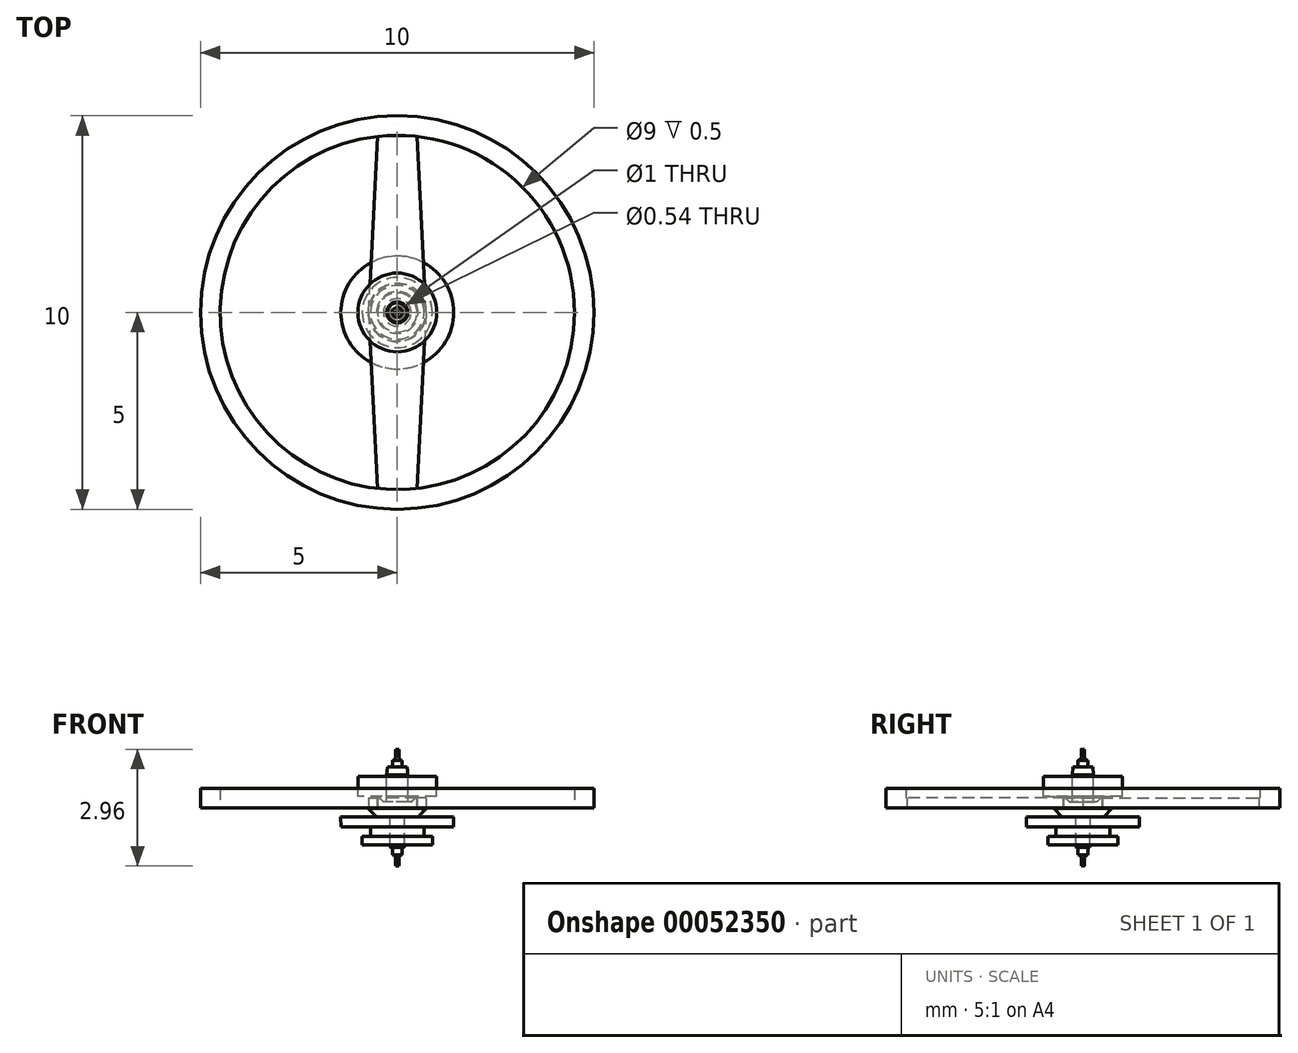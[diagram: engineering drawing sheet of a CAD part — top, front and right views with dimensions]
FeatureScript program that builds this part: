
annotation { "Feature Type Name" : "Feature", "Feature Type Description" : "" }
export const myFeature = defineFeature(function(context is Context, id is Id, definition is map)
    precondition{}
    {
        {
            var Q0;
            Q0=qCreatedBy(makeId("Front.planeOp"),FACE);
            var sketch = newSketch(context, id + "F0", { "sketchPlane" : qUnion([Q0])});
            skLineSegment(sketch, "E0", {"start": v(0, 0) * mm, "end": v(-0.04, 0) * mm});
            skLineSegment(sketch, "E1", {"start": v(-0.04, 0) * mm, "end": v(-0.04, 0.28) * mm});
            skLineSegment(sketch, "E2", {"start": v(-0.04, 0.28) * mm, "end": v(-0.12, 0.28) * mm});
            skLineSegment(sketch, "E3", {"start": v(-0.13, 0.28) * mm, "end": v(-0.13, 0.47) * mm});
            skLineSegment(sketch, "E4", {"start": v(-0.12, 0.47) * mm, "end": v(-0.17, 0.47) * mm});
            skLineSegment(sketch, "E5", {"start": v(-0.18, 0.48) * mm, "end": v(-0.18, 1.25) * mm});
            skLineSegment(sketch, "E6", {"start": v(-0.18, 1.25) * mm, "end": v(-0.53, 1.25) * mm});
            skLineSegment(sketch, "E7", {"start": v(-0.53, 1.25) * mm, "end": v(-0.74, 1.46) * mm});
            skLineSegment(sketch, "E8", {"start": v(-0.73, 1.47) * mm, "end": v(-0.5, 1.47) * mm});
            skLineSegment(sketch, "E9", {"start": v(-0.5, 1.47) * mm, "end": v(-0.5, 1.77) * mm});
            skLineSegment(sketch, "E10", {"start": v(-0.5, 1.77) * mm, "end": v(-0.35, 1.62) * mm});
            skLineSegment(sketch, "E11", {"start": v(-0.35, 1.62) * mm, "end": v(-0.27, 1.62) * mm});
            skLineSegment(sketch, "E12", {"start": v(-0.27, 1.62) * mm, "end": v(-0.27, 2.31) * mm});
            skLineSegment(sketch, "E13", {"start": v(-0.27, 2.3) * mm, "end": v(-0.25, 2.51) * mm});
            skLineSegment(sketch, "E14", {"start": v(-0.25, 2.51) * mm, "end": v(-0.12, 2.51) * mm});
            skLineSegment(sketch, "E15", {"start": v(-0.13, 2.51) * mm, "end": v(-0.13, 2.68) * mm});
            skLineSegment(sketch, "E16", {"start": v(-0.12, 2.68) * mm, "end": v(-0.04, 2.68) * mm});
            skLineSegment(sketch, "E17", {"start": v(-0.04, 2.68) * mm, "end": v(-0.04, 2.96) * mm});
            skLineSegment(sketch, "E18", {"start": v(-0.04, 2.96) * mm, "end": v(0, 2.96) * mm});
            skLineSegment(sketch, "E19", {"start": v(0, 2.96) * mm, "end": v(0, 0) * mm});
            skLineSegment(sketch, "E20", {"start": v(-0.73, 1.47) * mm, "end": v(-0.74, 1.46) * mm});
            skPoint(sketch, "E21.orphan", {"position": v(-0.75, 1.47) * mm});
            skLineSegment(sketch, "E22", {"start": v(-0.18, 0.48) * mm, "end": v(-0.17, 0.47) * mm});
            skPoint(sketch, "E23.orphan", {"position": v(-0.18, 0.47) * mm});
            skLineSegment(sketch, "E24", {"start": v(-0.27, 1.77) * mm, "end": v(-1, 1.77) * mm});
            skLineSegment(sketch, "E25", {"start": v(-1, 1.77) * mm, "end": v(-1, 2.27) * mm});
            skLineSegment(sketch, "E26", {"start": v(-1, 2.27) * mm, "end": v(-0.27, 2.27) * mm});
            skLineSegment(sketch, "E27", {"start": v(-0.18, 1.25) * mm, "end": v(-1.43, 1.24) * mm});
            skLineSegment(sketch, "E28", {"start": v(-1.43, 1.24) * mm, "end": v(-1.43, 1) * mm});
            skLineSegment(sketch, "E29", {"start": v(-1.43, 1) * mm, "end": v(-0.68, 1) * mm});
            skLineSegment(sketch, "E30", {"start": v(-0.68, 1) * mm, "end": v(-0.68, 0.75) * mm});
            skLineSegment(sketch, "E31", {"start": v(-0.68, 0.75) * mm, "end": v(-0.9, 0.75) * mm});
            skLineSegment(sketch, "E32", {"start": v(-0.9, 0.75) * mm, "end": v(-0.9, 0.54) * mm});
            skLineSegment(sketch, "E33", {"start": v(-0.9, 0.54) * mm, "end": v(-0.18, 0.54) * mm});
            skSolve(sketch);
        }
        {
            var Q0;
            Q0=makeQuery(id+"F0.imprint","IMPRINT",FACE,{"disambiguationData":[TD([[makeQuery(id+"F0.imprint","IMPRINT",EDGE,{"derivedFrom":sQuery(id+"F0.wireOp",EDGE,"E0")}),-1.0]])]});
            var Q1;
            Q1=sQuery(id+"F0.wireOp",EDGE,"E19");
            revolve(context, id + "F1", {"entities" : qUnion([Q0]), "axis" : qUnion([Q1]), "revolveType" : RevolveType.FULL});
        }
        {
            var Q0;
            Q0=makeQuery(id+"F1.opRevolve","SWEPT_EDGE",EDGE,{"disambiguationData":[OSD([sQuery(id+"F0.wireOp",EDGE,"E16"),sQuery(id+"F0.wireOp",EDGE,"E17")])]});
            fillet(context, id + "F2", {"entities" : qUnion([Q0]), "radius" : 0.1 * mm, "tangentPropagation" : true, "allowEdgeOverflow" : false});
        }
        {
            var Q0;
            Q0=makeQuery(id+"F1.opRevolve","SWEPT_EDGE",EDGE,{"disambiguationData":[OSD([sQuery(id+"F0.wireOp",EDGE,"E1"),sQuery(id+"F0.wireOp",EDGE,"E2")])]});
            fillet(context, id + "F3", {"entities" : qUnion([Q0]), "radius" : 0.1 * mm, "tangentPropagation" : true, "allowEdgeOverflow" : false});
        }
        {
            var Q0;
            Q0=makeQuery(id+"F1.opRevolve","SWEPT_FACE",FACE,{"disambiguationData":[OSD([sQuery(id+"F0.wireOp",EDGE,"E8")])]});
            var sketch = newSketch(context, id + "F4", { "sketchPlane" : qUnion([Q0])});
            skCircle(sketch, "E34.0", {"center": v(0, 0) * mm, "radius": 0.5 * mm});
            skCircle(sketch, "E35", {"center": v(0, 0) * mm, "radius": 5 * mm});
            skCircle(sketch, "E36", {"center": v(0, 0) * mm, "radius": 4.5 * mm});
            skCircle(sketch, "E37.0", {"center": v(0, 0) * mm, "radius": 0.73 * mm});
            skCircle(sketch, "E38", {"center": v(0, -4.5) * mm, "radius": 0.5 * mm, "construction": true});
            skCircle(sketch, "E39", {"center": v(0, 4.5) * mm, "radius": 0.5 * mm, "construction": true});
            skLineSegment(sketch, "E40", {"start": v(-0.73, 0) * mm, "end": v(-0.5, -4.47) * mm});
            skLineSegment(sketch, "E41", {"start": v(0.73, 0) * mm, "end": v(0.5, -4.47) * mm});
            skLineSegment(sketch, "E42", {"start": v(-0.73, 0) * mm, "end": v(-0.5, 4.47) * mm});
            skLineSegment(sketch, "E43", {"start": v(0.73, 0) * mm, "end": v(0.5, 4.47) * mm});
            skSolve(sketch);
        }
        {
            var Q0;
            Q0=makeQuery(id+"F4.imprint","IMPRINT",FACE,{"disambiguationData":[TD([[makeQuery(id+"F4.imprint","IMPRINT",EDGE,{"derivedFrom":sQuery(id+"F4.wireOp",EDGE,"E35")}),1.0]])]});
            var Q1;
            {var subQ0=sQuery(id+"F4.wireOp",EDGE,"6afa0338-6ddc-483a-af36-2ee9739ef733");var subQ1=sQuery(id+"F4.wireOp",EDGE,"E36");var subQ2=makeQuery(id+"F4.imprint","INTERSECT",VERTEX,{"derivedFrom":[subQ1,subQ0]});Q1=makeQuery(id+"F4.imprint","IMPRINT",FACE,{"disambiguationData":[TD([[makeQuery(id+"F4.imprint","IMPRINT",EDGE,{"disambiguationData":[TD([[subQ2,1.0]])],"derivedFrom":subQ1}),1.0]])]});}
            var Q2;
            {var subQ0=sQuery(id+"F4.wireOp",EDGE,"6afa0338-6ddc-483a-af36-2ee9739ef733");var subQ1=sQuery(id+"F4.wireOp",EDGE,"7b0f4a41-d3ac-4313-a1fa-f4f4589f324b");var subQ2=makeQuery(id+"F4.imprint","INTERSECT",VERTEX,{"derivedFrom":[subQ1,subQ0]});Q2=makeQuery(id+"F4.imprint","IMPRINT",FACE,{"disambiguationData":[TD([[makeQuery(id+"F4.imprint","IMPRINT",EDGE,{"disambiguationData":[TD([[subQ2,1.0]])],"derivedFrom":subQ1}),1.0]])]});}
            var Q3;
            {var subQ0=sQuery(id+"F4.wireOp",EDGE,"6afa0338-6ddc-483a-af36-2ee9739ef733");var subQ1=sQuery(id+"F4.wireOp",EDGE,"E34.0");var subQ2=makeQuery(id+"F4.imprint","INTERSECT",VERTEX,{"derivedFrom":[subQ1,subQ0,sQuery(id+"F4.wireOp",EDGE,"c907ba59-9a1e-415d-8a9b-9e27a359e78b")]});Q3=makeQuery(id+"F4.imprint","IMPRINT",FACE,{"disambiguationData":[TD([[makeQuery(id+"F4.imprint","IMPRINT",EDGE,{"disambiguationData":[TD([[subQ2,1.0]])],"derivedFrom":subQ1}),-1.0]])]});}
            var Q4;
            {var subQ0=sQuery(id+"F4.wireOp",EDGE,"80b41425-46ce-433e-b179-6af53ed49cd5");var subQ1=sQuery(id+"F4.wireOp",EDGE,"7b0f4a41-d3ac-4313-a1fa-f4f4589f324b");var subQ2=makeQuery(id+"F4.imprint","INTERSECT",VERTEX,{"derivedFrom":[subQ1,subQ0]});Q4=makeQuery(id+"F4.imprint","IMPRINT",FACE,{"disambiguationData":[TD([[makeQuery(id+"F4.imprint","IMPRINT",EDGE,{"disambiguationData":[TD([[subQ2,1.0]])],"derivedFrom":subQ1}),1.0]])]});}
            var Q5;
            {var subQ0=sQuery(id+"F4.wireOp",EDGE,"904a6068-8214-4e3a-808b-5e067327ec72");var subQ1=sQuery(id+"F4.wireOp",EDGE,"80b41425-46ce-433e-b179-6af53ed49cd5");var subQ2=makeQuery(id+"F4.imprint","INTERSECT",VERTEX,{"derivedFrom":[sQuery(id+"F4.wireOp",EDGE,"E34.0"),subQ1,subQ0]});Q5=makeQuery(id+"F4.imprint","IMPRINT",FACE,{"disambiguationData":[TD([[makeQuery(id+"F4.imprint","IMPRINT",EDGE,{"disambiguationData":[TD([[subQ2,-1.0]])],"derivedFrom":subQ1}),-1.0]])]});}
            var Q6;
            {var subQ0=sQuery(id+"F4.wireOp",EDGE,"c907ba59-9a1e-415d-8a9b-9e27a359e78b");var subQ1=sQuery(id+"F4.wireOp",EDGE,"E34.0");var subQ2=makeQuery(id+"F4.imprint","INTERSECT",VERTEX,{"derivedFrom":[subQ1,sQuery(id+"F4.wireOp",EDGE,"6afa0338-6ddc-483a-af36-2ee9739ef733"),subQ0]});Q6=makeQuery(id+"F4.imprint","IMPRINT",FACE,{"disambiguationData":[TD([[makeQuery(id+"F4.imprint","IMPRINT",EDGE,{"disambiguationData":[TD([[subQ2,-1.0]])],"derivedFrom":subQ1}),-1.0]])]});}
            var Q7;
            {var subQ0=sQuery(id+"F4.wireOp",EDGE,"c907ba59-9a1e-415d-8a9b-9e27a359e78b");var subQ1=sQuery(id+"F4.wireOp",EDGE,"7b0f4a41-d3ac-4313-a1fa-f4f4589f324b");var subQ2=makeQuery(id+"F4.imprint","INTERSECT",VERTEX,{"derivedFrom":[subQ1,subQ0]});Q7=makeQuery(id+"F4.imprint","IMPRINT",FACE,{"disambiguationData":[TD([[makeQuery(id+"F4.imprint","IMPRINT",EDGE,{"disambiguationData":[TD([[subQ2,-1.0]])],"derivedFrom":subQ1}),1.0]])]});}
            var Q8;
            {var subQ0=sQuery(id+"F4.wireOp",EDGE,"c907ba59-9a1e-415d-8a9b-9e27a359e78b");var subQ1=sQuery(id+"F4.wireOp",EDGE,"6afa0338-6ddc-483a-af36-2ee9739ef733");var subQ2=makeQuery(id+"F4.imprint","INTERSECT",VERTEX,{"derivedFrom":[sQuery(id+"F4.wireOp",EDGE,"E34.0"),subQ1,subQ0]});Q8=makeQuery(id+"F4.imprint","IMPRINT",FACE,{"disambiguationData":[TD([[makeQuery(id+"F4.imprint","IMPRINT",EDGE,{"disambiguationData":[TD([[subQ2,-1.0]])],"derivedFrom":subQ1}),1.0]])]});}
            var Q9;
            {var subQ0=sQuery(id+"F4.wireOp",EDGE,"6afa0338-6ddc-483a-af36-2ee9739ef733");var subQ1=sQuery(id+"F4.wireOp",EDGE,"7b0f4a41-d3ac-4313-a1fa-f4f4589f324b");var subQ2=makeQuery(id+"F4.imprint","INTERSECT",VERTEX,{"derivedFrom":[subQ1,subQ0]});Q9=makeQuery(id+"F4.imprint","IMPRINT",FACE,{"disambiguationData":[TD([[makeQuery(id+"F4.imprint","IMPRINT",EDGE,{"disambiguationData":[TD([[subQ2,-1.0]])],"derivedFrom":subQ1}),1.0]])]});}
            var Q10;
            {var subQ0=sQuery(id+"F4.wireOp",EDGE,"c907ba59-9a1e-415d-8a9b-9e27a359e78b");var subQ1=sQuery(id+"F4.wireOp",EDGE,"E36");var subQ2=makeQuery(id+"F4.imprint","INTERSECT",VERTEX,{"derivedFrom":[subQ1,subQ0]});Q10=makeQuery(id+"F4.imprint","IMPRINT",FACE,{"disambiguationData":[TD([[makeQuery(id+"F4.imprint","IMPRINT",EDGE,{"disambiguationData":[TD([[subQ2,-1.0]])],"derivedFrom":subQ1}),1.0]])]});}
            var Q11;
            Q11=makeQuery(id+"F4.imprint","IMPRINT",FACE,{"disambiguationData":[TD([[makeQuery(id+"F4.imprint","IMPRINT",EDGE,{"derivedFrom":sQuery(id+"F4.wireOp",EDGE,"E34.0")}),-1.0]])]});
            extrude(context, id + "F5", {"entities" : qUnion([Q0, Q1, Q2, Q3, Q4, Q5, Q6, Q7, Q8, Q9, Q10, Q11]), "depth" : 0.25 * mm});
        }
        {
            var Q0;
            Q0=makeQuery(id+"F4.imprint","IMPRINT",FACE,{"disambiguationData":[TD([[makeQuery(id+"F4.imprint","IMPRINT",EDGE,{"derivedFrom":sQuery(id+"F4.wireOp",EDGE,"E35")}),1.0]])]});
            extrude(context, id + "F6", {"entities" : qUnion([Q0]), "operationType" : NewBodyOperationType.ADD, "depth" : 0.5 * mm});
        }
        {
            var Q0;
            {var subQ2=sQuery(id+"F0.wireOp",EDGE,"E25");Q0=makeQuery(id+"F0.imprint","IMPRINT",FACE,{"disambiguationData":[TD([[makeQuery(id+"F0.imprint","IMPRINT",EDGE,{"derivedFrom":subQ2}),-1.0]])]});}
            var Q1;
            Q1=sQuery(id+"F0.wireOp",EDGE,"E19");
            revolve(context, id + "F7", {"entities" : qUnion([Q0]), "axis" : qUnion([Q1]), "revolveType" : RevolveType.FULL});
        }
        {
            var Q0;
            {var subQ0=sQuery(id+"F0.wireOp",EDGE,"E27");Q0=makeQuery(id+"F0.imprint","IMPRINT",FACE,{"disambiguationData":[TD([[makeQuery(id+"F0.imprint","IMPRINT",EDGE,{"derivedFrom":subQ0}),1.0]])]});}
            var Q1;
            Q1=sQuery(id+"F0.wireOp",EDGE,"E19");
            revolve(context, id + "F8", {"entities" : qUnion([Q0]), "axis" : qUnion([Q1]), "revolveType" : RevolveType.FULL});
        }
    });
